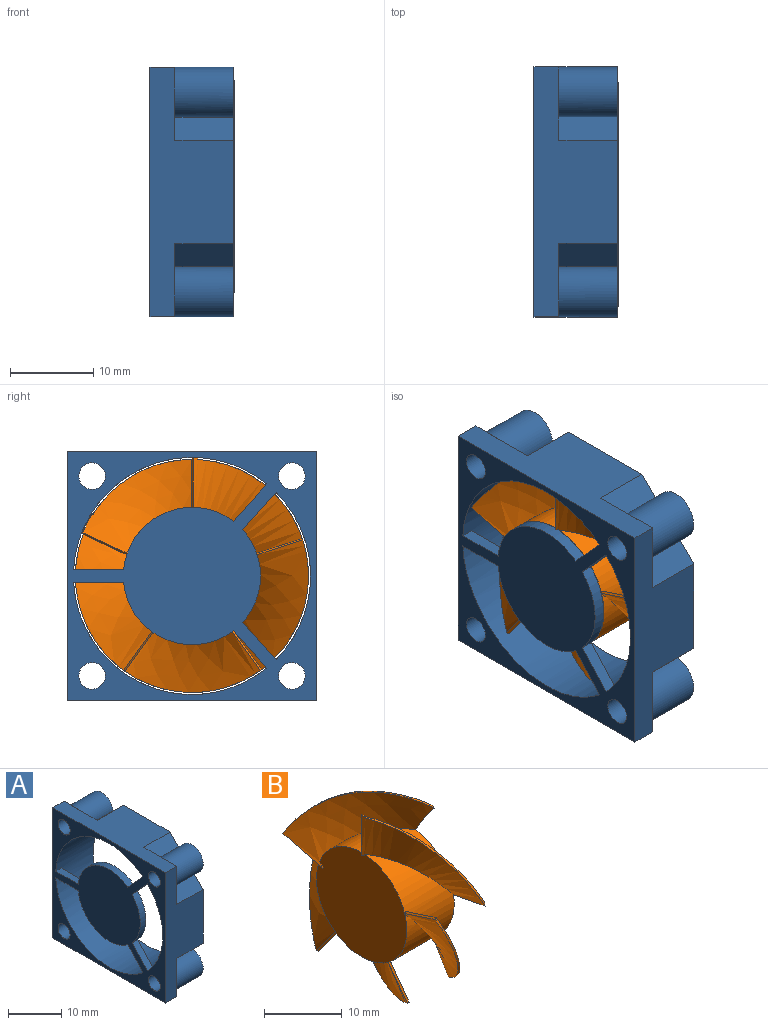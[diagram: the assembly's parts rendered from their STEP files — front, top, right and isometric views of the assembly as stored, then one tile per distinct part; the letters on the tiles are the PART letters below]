
ASSEMBLY  parts=2 mates=1
PART A: 45 faces, bbox 10x30x30 mm
  f0: plane 30x10mm, normal (0,1,0), area 177mm2, adj f2,f6,f10,f18,f19,f24,f25,f40
  f1: cylinder r=1.6mm len=10mm, axis (1,0,0), area 100.5mm2, adj f6,f24
  f2: plane 30x10mm, normal (0,0,-1), area 177mm2, adj f0,f6,f8,f9,f11,f15,f16,f24
  f3: plane 5.79x2.79mm, normal (1,0,0), area 5.8mm2, adj f9,f12,f23
  f4: plane 3x3mm, normal (1,0,0), area 1.9mm2, adj f9,f23,f25
  f5: plane 5.79x2.79mm, normal (1,0,0), area 5.8mm2, adj f9,f13,f14
  f6: plane 30x30mm, normal (-1,0,0), area 470.7mm2, adj f0,f1,f2,f7,f9,f25,f26,f27
  f7: cylinder r=1.6mm len=10mm, axis (1,0,0), area 100.5mm2, adj f6,f24
  f8: plane 3x3mm, normal (1,0,0), area 1.9mm2, adj f2,f9,f14
  f9: plane 30x10mm, normal (0,-1,0), area 177mm2, adj f2,f3,f4,f5,f6,f8,f12,f13
  f10: plane 5.79x2.79mm, normal (1,0,0), area 5.8mm2, adj f0,f19,f20
  f11: plane 5.79x2.79mm, normal (1,0,0), area 5.8mm2, adj f2,f14,f15
  f12: plane 7x2.79mm, normal (0,-0.71,0.71), area 27.7mm2, adj f3,f9,f23,f24
  f13: plane 7x2.79mm, normal (0,-0.71,-0.71), area 27.7mm2, adj f5,f9,f14,f24
  f14: cylinder r=3mm len=7mm, axis (1,0,0), area 96.1mm2, adj f5,f8,f11,f13,f15,f24
  f15: plane 7x2.79mm, normal (0,-0.71,-0.71), area 27.7mm2, adj f2,f11,f14,f24
  f16: plane 7x2.79mm, normal (0,0.71,-0.71), area 27.7mm2, adj f2,f17,f24,f44
  f17: cylinder r=3mm len=7mm, axis (1,0,0), area 96.1mm2, adj f16,f18,f24,f42,f43,f44
  f18: plane 7x2.79mm, normal (0,0.71,-0.71), area 27.7mm2, adj f0,f17,f24,f42
  f19: plane 7x2.79mm, normal (0,0.71,0.71), area 27.7mm2, adj f0,f10,f20,f24
  f20: cylinder r=3mm len=7mm, axis (1,0,0), area 96.1mm2, adj f10,f19,f21,f24,f39,f40
  f21: plane 7x2.79mm, normal (0,0.71,0.71), area 27.7mm2, adj f20,f24,f25,f39
  f22: plane 7x2.79mm, normal (0,-0.71,0.71), area 27.7mm2, adj f23,f24,f25,f41
  f23: cylinder r=3mm len=7mm, axis (1,0,0), area 96.1mm2, adj f3,f4,f12,f22,f24,f41
  f24: plane 30x30mm, normal (1,0,0), area 175.7mm2, adj f0,f1,f2,f7,f9,f12,f13,f14
  f25: plane 30x10mm, normal (0,0,1), area 177mm2, adj f0,f4,f6,f9,f21,f22,f24,f39
  f26: cylinder r=14.25mm len=28.5mm, axis (1,0,0), area 888.6mm2, adj f6,f24,f29,f30,f33,f35,f36,f37
  f27: cylinder r=1.6mm len=10mm, axis (1,0,0), area 100.5mm2, adj f6,f24
  f28: cylinder r=1.6mm len=10mm, axis (1,0,0), area 100.5mm2, adj f6,f24
  f29: plane 6.01x1.5mm, normal (0,0,1), area 9mm2, adj f6,f26,f31,f38
  f30: plane 6.01x1.5mm, normal (0,0,-1), area 9mm2, adj f6,f26,f34,f38
  f31: cylinder r=8.25mm len=13.17mm, axis (1,0,0), area 26.3mm2, adj f6,f29,f37,f38
  f32: cylinder r=8.25mm len=11.18mm, axis (1,0,0), area 18.4mm2, adj f6,f33,f36,f38
  f33: plane 4.46x4.03mm, normal (0,-0.74,-0.67), area 9mm2, adj f6,f26,f32,f38
  f34: cylinder r=8.25mm len=13.17mm, axis (1,0,0), area 26.3mm2, adj f6,f30,f35,f38
  f35: plane 4.46x4.03mm, normal (0,0.74,-0.67), area 9mm2, adj f6,f26,f34,f38
  f36: plane 4.46x4.03mm, normal (0,-0.74,0.67), area 9mm2, adj f6,f26,f32,f38
  f37: plane 4.46x4.03mm, normal (0,0.74,0.67), area 9mm2, adj f6,f26,f31,f38
  f38: plane 24.35x22.11mm, normal (1,0,0), area 240.8mm2, adj f26,f29,f30,f31,f32,f33,f34,f35
  f39: plane 5.79x2.79mm, normal (1,0,0), area 5.8mm2, adj f20,f21,f25
  f40: plane 3x3mm, normal (1,0,0), area 1.9mm2, adj f0,f20,f25
  f41: plane 5.79x2.79mm, normal (1,0,0), area 5.8mm2, adj f22,f23,f25
  f42: plane 5.79x2.79mm, normal (1,0,0), area 5.8mm2, adj f0,f17,f18
  f43: plane 3x3mm, normal (1,0,0), area 1.9mm2, adj f0,f2,f17
  f44: plane 5.79x2.79mm, normal (1,0,0), area 5.8mm2, adj f2,f16,f17
PART B: 33 faces, bbox 10.9x28.7x28.8 mm
  f0: plane 26.97x25.52mm, normal (1,0,0), area 228.4mm2, adj f1,f6,f8,f9,f10,f11,f12,f14
  f1: bspline ~16.32x9.32mm, area 97.6mm2, adj f0,f2,f10,f31
  f2: plane 4.8x3.56mm, normal (-0.61,-0.64,-0.46), area 1.7mm2, adj f1,f10,f20,f31
  f3: bspline ~2.5x1.41mm, area 0.8mm2, adj f4,f9,f18,f19
  f4: plane 0.7x0.42mm, normal (1,0,0), area 0.1mm2, adj f3,f9,f19,f28
  f5: plane 6.19x0.24mm, normal (-0.61,0.79,0), area 1.8mm2, adj f7,f15,f16,f30,f32
  f6: cylinder r=14mm len=13.79mm, axis (-1,0,0), area 6.1mm2, adj f0,f15,f30,f32
  f7: cylinder r=14.82mm len=0.75mm, axis (0.99,0.15,0), area 0.1mm2, adj f5,f15,f30
  f8: cylinder r=8.2mm len=14.98mm, axis (1,0,0), area 80.2mm2, adj f0,f13,f24,f25,f30
  f9: bspline ~17.8x11.77mm, area 111.1mm2, adj f0,f3,f4,f12,f13,f17,f18,f28
  f10: cylinder r=8.2mm len=13.02mm, axis (1,0,0), area 84.4mm2, adj f0,f1,f2,f13,f21
  f11: cylinder r=8.2mm len=13.24mm, axis (1,0,0), area 84.4mm2, adj f0,f13,f22,f23,f26
  f12: cylinder r=8.2mm len=15.63mm, axis (1,0,0), area 84.3mm2, adj f0,f9,f13,f32
  f13: plane 16.4x16.4mm, normal (-1,0,0), area 211mm2, adj f8,f9,f10,f11,f12,f14,f16,f17
  f14: cylinder r=8.2mm len=14.83mm, axis (1,0,0), area 88.5mm2, adj f0,f13,f19,f20
  f15: plane 0.72x0.22mm, normal (1,0,0), area 0.1mm2, adj f5,f6,f7,f30
  f16: bspline ~0.49x0.47mm, area 0.1mm2, adj f5,f13,f30
  f17: bspline ~0.88x0.32mm, area 0.1mm2, adj f9,f13,f18
  f18: plane 6.21x2.88mm, normal (-0.61,0.24,-0.75), area 1.9mm2, adj f3,f9,f17,f19
  f19: bspline ~17.18x11.56mm, area 108.1mm2, adj f0,f3,f4,f14,f18,f28
  f20: bspline ~16.87x9.18mm, area 100.4mm2, adj f0,f2,f14,f31
  f21: bspline ~17.47x8.59mm, area 100.4mm2, adj f0,f10,f26,f29
  f22: bspline ~18.71x9.2mm, area 97.6mm2, adj f0,f11,f26,f29
  f23: bspline ~17.47x11.48mm, area 100.4mm2, adj f0,f11,f25,f27
  f24: bspline ~17.33x11.26mm, area 97.6mm2, adj f0,f8,f25,f27
  f25: plane 5.58x1.97mm, normal (-0.61,0.24,0.75), area 1.7mm2, adj f8,f23,f24,f27
  f26: plane 4.8x3.56mm, normal (-0.61,-0.64,0.46), area 1.7mm2, adj f11,f21,f22,f29
  f27: cylinder r=14mm len=16.54mm, axis (-1,0,0), area 6mm2, adj f0,f23,f24,f25
  f28: cylinder r=14mm len=16.86mm, axis (-1,0,0), area 6mm2, adj f0,f4,f9,f19
  f29: cylinder r=14mm len=17.62mm, axis (-1,0,0), area 6mm2, adj f0,f21,f22,f26
  f30: bspline ~13.81x12.91mm, area 103.3mm2, adj f0,f5,f6,f7,f8,f13,f15,f16
  f31: cylinder r=14mm len=16.97mm, axis (-1,0,0), area 6mm2, adj f0,f1,f2,f20
  f32: bspline ~14.15x13.49mm, area 100.4mm2, adj f0,f5,f6,f12
PLACE A t=(-7.19,-2.42,3.82)mm
PLACE B t=(-7.19,-2.41,3.83)mm
MATE fastened B.f6 <-> A.f26  axis (-1,0,0) through (-5.69,-2.42,3.82)mm
